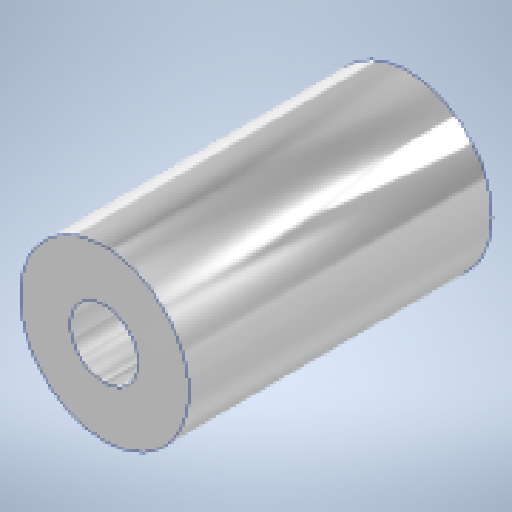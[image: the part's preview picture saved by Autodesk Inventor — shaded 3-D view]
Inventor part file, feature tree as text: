
AUTODESK INVENTOR PART (.ipt)
format: ipt  version: 2024.1 (Build 281209000, 209)  size: 276,480 bytes
history: native  units: in
note: dims shown in document units (in); Inventor stores cm internally (conversion verified against a paired STEP export)
features: extrude x2, sketch x2
ambient origin geometry x8: Origin, YZ Plane, XZ Plane, XY Plane, X Axis, Y Axis, Z Axis, Center Point
bodies: Solid1 (feature_tree)
feature tree (4):
  extrude  "Extrusion1"  Depth=0.3937in
  extrude  "Extrusion2"  Depth=0.3543in
  sketch  "Sketch1"  dims[d0=0.3937in d1=0.1181in]
  sketch  "Sketch2"  dims[d2=0.7087in d3=0.0in d4=0.1575in d5=0.3543in d6=0.0in]
